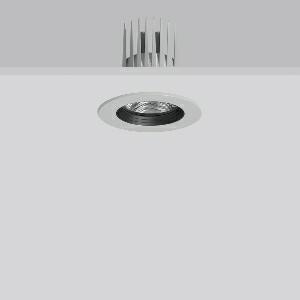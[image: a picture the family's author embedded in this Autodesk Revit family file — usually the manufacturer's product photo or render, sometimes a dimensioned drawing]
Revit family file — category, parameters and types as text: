
# Revit family: heledon_mini_e_901748_004_3_98a6
name_source: partatom
category: Lighting Fixtures
units: mm (PartAtom-declared; Revit-internal decimal feet)

## family parameters
Cut with Voids When Loaded = No
Host = Face
Light Source = No
Part Type = Normal
Room Calculation Point = No
Round Connector Dimension = Use Diameter
Shared = No

## types (1)
- HELEDON mini E (1 x LED Modul 935, 3700 lm, 3500)
    Apparent Load = 29 VA
    Approval mark = CE
    CIE Flux Codes = 100 100 100 100 100
    Color Rendering = 92
    Color Temperature = 3500
    Default Elevation = 1800 mm
    Description = Series: HELEDON mini
Round recessed downlight. Housing: die-cast aluminium, powder-coated. Black plastic ring and recessed LED to prevent glare from the side. Optical assembly with reflector made of MIRO-Silver with 98% total light reflection for outstanding efficiency - can be changed without tools. Best colour rendering index Ra>90. Suitable for Recessed ceiling mounting. Installation without tools thanks to spring fastening system. Including separate LED converter with connecting cable 600 mm.High quality converter without flickering and stroboscopic effect. Through-wiring box (5 pole) available as accessory. The following accessories can be mounted without use of tools: interchangeable lenses, decorative glasses, honeycomb louvre, clear and frosted diffusers, white interchangeable plastic ring. 
Colour: silver
Diameter: 124 mm
Height: 3 mm
Cut-out diameter: 114 mm
Recess height: 170 mm
Luminaire: recess height: 120 mm
Lamp: LED
Socket: without socket
Colour temperature: 3500K
Colour rendering index (CRI): 92
System power: 29 W
Rated luminous flux: 3700 lm
Luminous efficiency: 128 lm/W
Control gear: Regulated power supply
Protection class: II
Type of protection: IP 20
    Height = 0 mm  [stored 0 ft]
    Lamp = 1 x LED Modul 935
    Lamp Light Flux = 3700 lm
    Lamp count = 1
    Length = 124 mm  [stored 0.406824 ft]
    Lifetime = 50000 h
    Luminous efficacy = 128 lm/W
    Manufacturer = RZB
    ModVariant = No
    Model = 901748.004.3
    Mounting Place = Ceiling
    Mounting Type = Recessed
    Number of Poles = 1
    OnlyDefault = Yes
    Power Factor = 1
    Product Name = HELEDON mini E
    Product group = Recessed downlights
    ProductGroupID = 402
    Protection Class = Protection class II
    Protection Degree = IP 20
    RLX_Detail_Level = 1
    RLX_Emergency_Light_Flux = 0 lm
    RLX_Emergency_Type = 0
    RLX_Emergency_Type_DB = No
    RlxData = <blob elided: 128157 chars, md5=118f00eb>
    Socket = socket
    Standby Power = 0 W
    System Light Flux = 3700 lm
    System Power = 29 W
    Type Comments = Product without accessories
    Type Image = 901657.004.jpg
    URL = http://relux.com
    VarID = ---
    Voltage = 230 V
    Voltage Range = 220-240 V
    Weight = 0.00 kg
    Width = 0 mm  [stored 0 ft]

note: [stored X ft] marks values corroborated as IEEE doubles in the binary element streams (Revit-internal decimal feet)

## geometry (parser evidence)
native form markers: Blend x4, Sweep x12
no freeform markers — native parametric forms only
